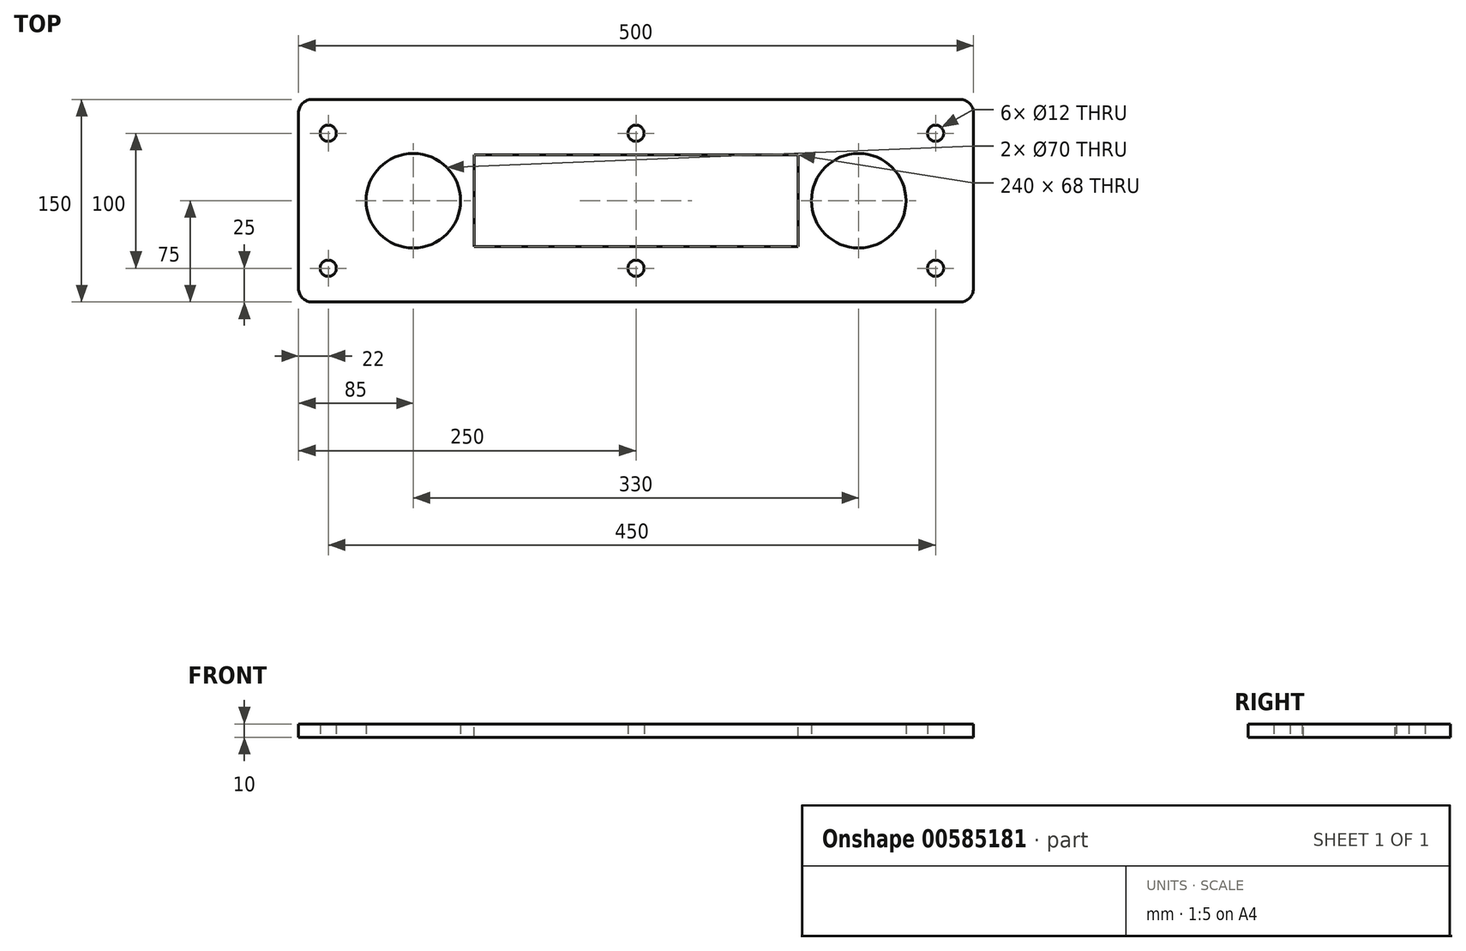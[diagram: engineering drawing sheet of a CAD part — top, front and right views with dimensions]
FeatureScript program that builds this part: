
annotation { "Feature Type Name" : "Feature", "Feature Type Description" : "" }
export const myFeature = defineFeature(function(context is Context, id is Id, definition is map)
    precondition{}
    {
        {
            var Q0;
            Q0=qCreatedBy(makeId("Top.planeOp"),FACE);
            var sketch = newSketch(context, id + "F0", { "sketchPlane" : qUnion([Q0])});
            skLineSegment(sketch, "E0.bottom", {"start": v(10, 0) * mm, "end": v(490, 0) * mm});
            skLineSegment(sketch, "E0.top", {"start": v(10, 150) * mm, "end": v(490, 150) * mm});
            skLineSegment(sketch, "E0.left", {"start": v(0, 10) * mm, "end": v(0, 140) * mm});
            skLineSegment(sketch, "E0.right", {"start": v(500, 10) * mm, "end": v(500, 140) * mm});
            skPoint(sketch, "E1.visualSharp", {"position": v(0, 150) * mm});
            skArc(sketch, "E1.filletArc", {"start": v(10, 150) * mm, "mid": v(2.93, 147.07) * mm, "end": v(0, 140) * mm});
            skPoint(sketch, "E2.visualSharp", {"position": v(500, 150) * mm});
            skArc(sketch, "E2.filletArc", {"start": v(500, 140) * mm, "mid": v(497.07, 147.07) * mm, "end": v(490, 150) * mm});
            skPoint(sketch, "E3.visualSharp", {"position": v(500, 0) * mm});
            skArc(sketch, "E3.filletArc", {"start": v(490, 0) * mm, "mid": v(497.07, 2.93) * mm, "end": v(500, 10) * mm});
            skPoint(sketch, "E4.visualSharp", {"position": v(0, 0) * mm});
            skArc(sketch, "E4.filletArc", {"start": v(0, 10) * mm, "mid": v(2.93, 2.93) * mm, "end": v(10, 0) * mm});
            skCircle(sketch, "E5", {"center": v(85, 75) * mm, "radius": 35 * mm});
            skCircle(sketch, "E6", {"center": v(415, 75) * mm, "radius": 35 * mm});
            skCircle(sketch, "E7", {"center": v(22, 125) * mm, "radius": 6 * mm});
            skCircle(sketch, "E8", {"center": v(472, 125) * mm, "radius": 6 * mm});
            skCircle(sketch, "E9", {"center": v(250, 125) * mm, "radius": 6 * mm});
            skCircle(sketch, "E10", {"center": v(472, 25) * mm, "radius": 6 * mm});
            skCircle(sketch, "E11", {"center": v(250, 25) * mm, "radius": 6 * mm});
            skCircle(sketch, "E12", {"center": v(22, 25) * mm, "radius": 6 * mm});
            skLineSegment(sketch, "E13.bottom", {"start": v(65, 0) * mm, "end": v(105, 0) * mm});
            skLineSegment(sketch, "E13.top", {"start": v(65, -15) * mm, "end": v(105, -15) * mm, "construction": true});
            skLineSegment(sketch, "E13.left", {"start": v(65, 0) * mm, "end": v(65, -15) * mm, "construction": true});
            skLineSegment(sketch, "E13.right", {"start": v(105, 0) * mm, "end": v(105, -15) * mm, "construction": true});
            skLineSegment(sketch, "E14.bottom", {"start": v(230, 0) * mm, "end": v(270, 0) * mm});
            skLineSegment(sketch, "E14.top", {"start": v(230, -15) * mm, "end": v(270, -15) * mm, "construction": true});
            skLineSegment(sketch, "E14.left", {"start": v(230, 0) * mm, "end": v(230, -15) * mm, "construction": true});
            skLineSegment(sketch, "E14.right", {"start": v(270, 0) * mm, "end": v(270, -15) * mm, "construction": true});
            skLineSegment(sketch, "E15.bottom", {"start": v(395, 0) * mm, "end": v(435, 0) * mm});
            skLineSegment(sketch, "E15.top", {"start": v(395, -15) * mm, "end": v(435, -15) * mm, "construction": true});
            skLineSegment(sketch, "E15.left", {"start": v(395, 0) * mm, "end": v(395, -15) * mm, "construction": true});
            skLineSegment(sketch, "E15.right", {"start": v(435, 0) * mm, "end": v(435, -15) * mm, "construction": true});
            skLineSegment(sketch, "E16.bottom", {"start": v(65, 150) * mm, "end": v(105, 150) * mm});
            skLineSegment(sketch, "E16.top", {"start": v(65, 165) * mm, "end": v(105, 165) * mm, "construction": true});
            skLineSegment(sketch, "E16.left", {"start": v(65, 150) * mm, "end": v(65, 165) * mm, "construction": true});
            skLineSegment(sketch, "E16.right", {"start": v(105, 150) * mm, "end": v(105, 165) * mm, "construction": true});
            skLineSegment(sketch, "E17.bottom", {"start": v(230, 150) * mm, "end": v(270, 150) * mm});
            skLineSegment(sketch, "E17.top", {"start": v(230, 165) * mm, "end": v(270, 165) * mm, "construction": true});
            skLineSegment(sketch, "E17.left", {"start": v(230, 150) * mm, "end": v(230, 165) * mm, "construction": true});
            skLineSegment(sketch, "E17.right", {"start": v(270, 150) * mm, "end": v(270, 165) * mm, "construction": true});
            skLineSegment(sketch, "E18.bottom", {"start": v(395, 150) * mm, "end": v(435, 150) * mm});
            skLineSegment(sketch, "E18.top", {"start": v(395, 165) * mm, "end": v(435, 165) * mm, "construction": true});
            skLineSegment(sketch, "E18.left", {"start": v(395, 150) * mm, "end": v(395, 165) * mm, "construction": true});
            skLineSegment(sketch, "E18.right", {"start": v(435, 150) * mm, "end": v(435, 165) * mm, "construction": true});
            skPoint(sketch, "E19", {"position": v(85, -15) * mm});
            skPoint(sketch, "E20", {"position": v(250, -15) * mm});
            skPoint(sketch, "E21", {"position": v(415, -15) * mm});
            skSolve(sketch);
        }
        {
            var Q0;
            Q0=qSketchRegion(id+"F0",true);
            extrude(context, id + "F1", {"entities" : qUnion([Q0]), "depth" : 10 * mm, "offsetDistance" : 25 * mm});
        }
        {
            var Q0;
            Q0=makeQuery(id+"F1.opExtrude","CAP_FACE",FACE,{"disambiguationData":[OSD([sQuery(id+"F0.wireOp",EDGE,"E0.bottom"),sQuery(id+"F0.wireOp",EDGE,"E0.top"),sQuery(id+"F0.wireOp",EDGE,"E0.left"),sQuery(id+"F0.wireOp",EDGE,"E0.right"),sQuery(id+"F0.wireOp",EDGE,"E1.filletArc"),sQuery(id+"F0.wireOp",EDGE,"E2.filletArc"),sQuery(id+"F0.wireOp",EDGE,"E3.filletArc"),sQuery(id+"F0.wireOp",EDGE,"E4.filletArc"),sQuery(id+"F0.wireOp",EDGE,"E5"),sQuery(id+"F0.wireOp",EDGE,"E6"),sQuery(id+"F0.wireOp",EDGE,"E7"),sQuery(id+"F0.wireOp",EDGE,"E8"),sQuery(id+"F0.wireOp",EDGE,"E9"),sQuery(id+"F0.wireOp",EDGE,"E10"),sQuery(id+"F0.wireOp",EDGE,"E11"),sQuery(id+"F0.wireOp",EDGE,"E12"),sQuery(id+"F0.wireOp",EDGE,"E13.bottom"),sQuery(id+"F0.wireOp",EDGE,"E14.bottom"),sQuery(id+"F0.wireOp",EDGE,"E15.bottom"),sQuery(id+"F0.wireOp",EDGE,"E16.bottom"),sQuery(id+"F0.wireOp",EDGE,"E17.bottom"),sQuery(id+"F0.wireOp",EDGE,"E18.bottom")])],"isStart":false});
            var sketch = newSketch(context, id + "F2", { "sketchPlane" : qUnion([Q0])});
            skLineSegment(sketch, "E22.bottom", {"start": v(130, 41) * mm, "end": v(370, 41) * mm});
            skLineSegment(sketch, "E22.top", {"start": v(130, 109) * mm, "end": v(370, 109) * mm});
            skLineSegment(sketch, "E22.left", {"start": v(130, 41) * mm, "end": v(130, 109) * mm});
            skLineSegment(sketch, "E22.right", {"start": v(370, 41) * mm, "end": v(370, 109) * mm});
            skSolve(sketch);
        }
        {
            var Q0;
            Q0 = qSketchRegion(id + "F2", true);
            extrude(context, id + "F3", {"entities" : qUnion([Q0]), "operationType" : NewBodyOperationType.REMOVE, "oppositeDirection" : true, "depth" : 25 * mm, "offsetDistance" : 25 * mm});
        }
    });
